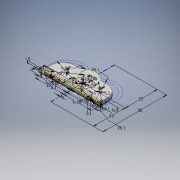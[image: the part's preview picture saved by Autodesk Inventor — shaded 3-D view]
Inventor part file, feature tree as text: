
AUTODESK INVENTOR PART (.ipt)
format: ipt  version: 2016 (Build 200138000, 138)  size: 246,272 bytes
history: native  units: mm
features: extrude x8, other x3, hole x2, sketch x1, projected_geometry x1
ambient origin geometry x8: Origin, YZ Plane, XZ Plane, XY Plane, X Axis, Y Axis, Z Axis, Center Point
bodies: Body1 (feature_tree)
feature tree (15):
  other  "ソリッド1"
  other  "構築線"
  extrude  "外形作成"  Depth=17.0mm
  extrude  "押し出し4"  Depth=5.6mm
  other  "固定具"
  hole  "穴1"  [1 undecoded]
  hole  "穴2"  [1 undecoded]
  extrude  "押し出し5"  Depth=8.6mm
  extrude  "押し出し6"  TaperAngle=0.0deg  [1 undecoded]
  extrude  "押し出し7"  Depth=20.1mm
  extrude  "押し出し8"  TaperAngle=0.0deg  [1 undecoded]
  extrude  "押し出し9"  Depth=25.0mm
  extrude  "押し出し10"  Depth=3.0mm
  sketch  "スケッチ6"
  projected_geometry  "投影ループ1"
note: 4 required parameter values undecoded (feature->parameter linkage not recoverable at this tier; creation-order binding heuristic only, values carry confidence <= 0.55)
